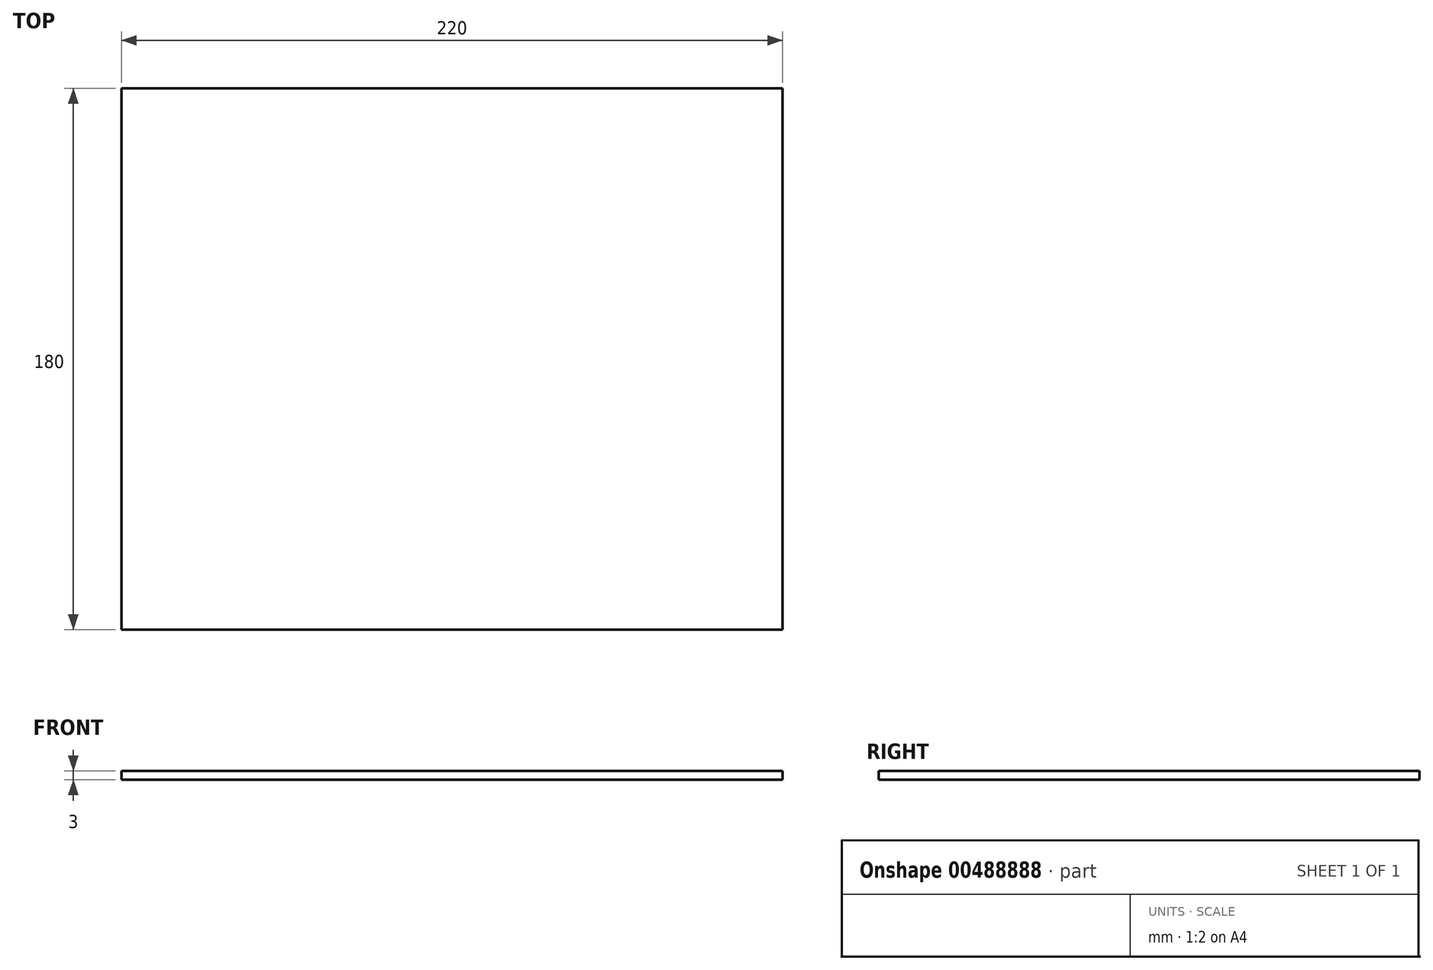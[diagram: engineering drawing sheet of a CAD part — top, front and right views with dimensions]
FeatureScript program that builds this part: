
annotation { "Feature Type Name" : "Feature", "Feature Type Description" : "" }
export const myFeature = defineFeature(function(context is Context, id is Id, definition is map)
    precondition{}
    {
        {
            var Q0;
            Q0=qCreatedBy(makeId("Top.planeOp"),FACE);
            var sketch = newSketch(context, id + "F0", { "sketchPlane" : qUnion([Q0])});
            skLineSegment(sketch, "E0.bottom", {"start": v(-105.13, 69.8) * mm, "end": v(114.87, 69.8) * mm});
            skLineSegment(sketch, "E0.top", {"start": v(-105.13, -110.2) * mm, "end": v(114.87, -110.2) * mm});
            skLineSegment(sketch, "E0.left", {"start": v(-105.13, 69.8) * mm, "end": v(-105.13, -110.2) * mm});
            skLineSegment(sketch, "E0.right", {"start": v(114.87, 69.8) * mm, "end": v(114.87, -110.2) * mm});
            skSolve(sketch);
        }
        {
            var Q0;
            Q0=makeQuery(id+"F0.imprint","IMPRINT",FACE,{"disambiguationData":[TD([[makeQuery(id+"F0.imprint","IMPRINT",EDGE,{"derivedFrom":sQuery(id+"F0.wireOp",EDGE,"E0.bottom")}),-1.0]])]});
            extrude(context, id + "F1", {"entities" : qUnion([Q0]), "depth" : 3 * mm});
        }
    });
